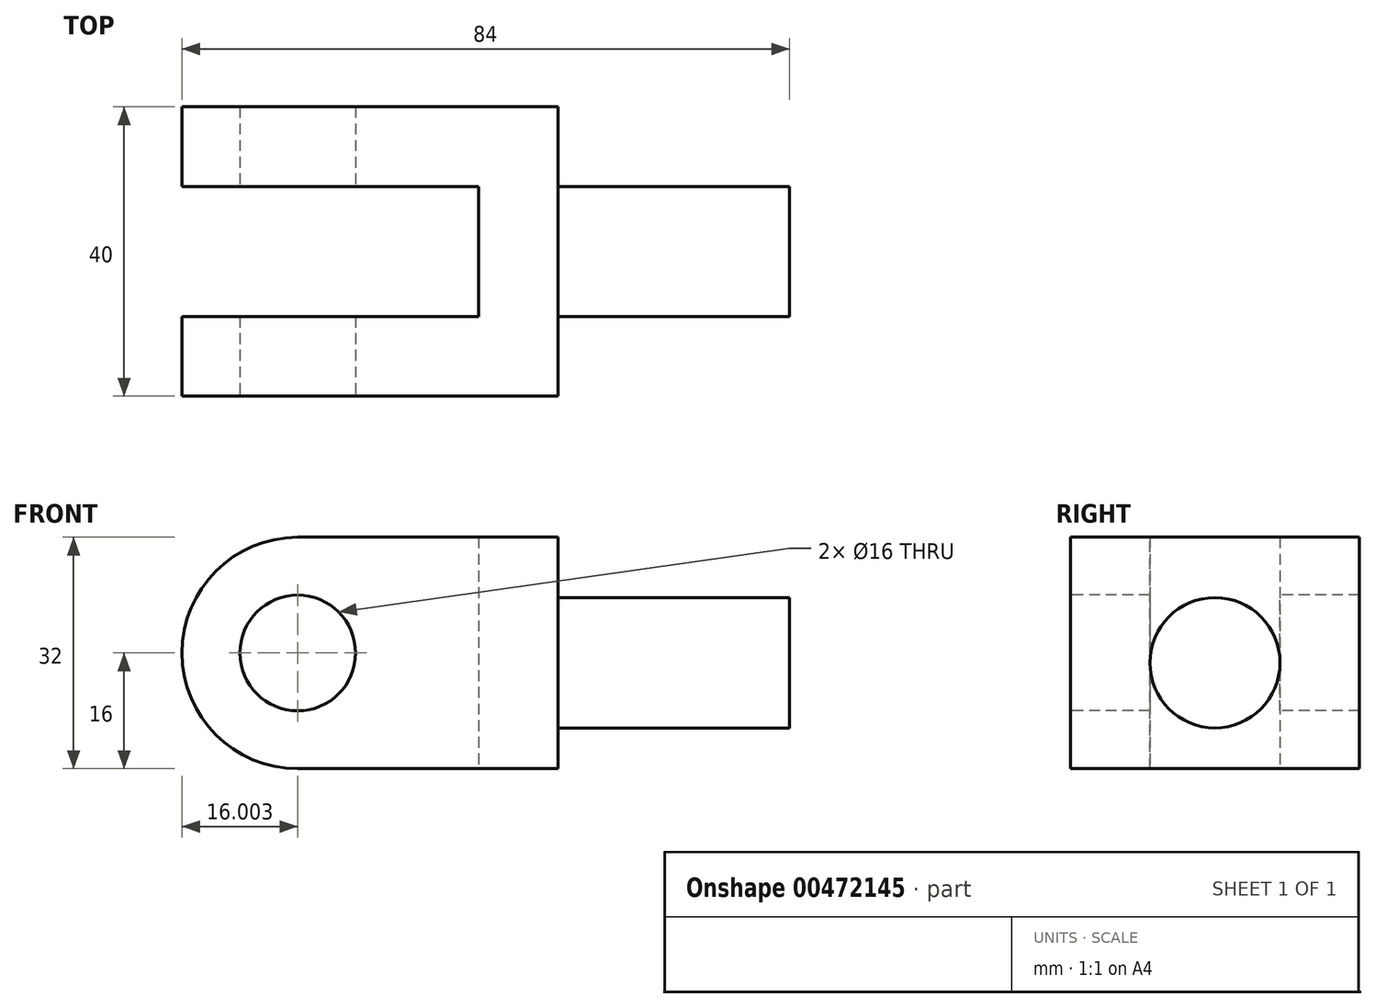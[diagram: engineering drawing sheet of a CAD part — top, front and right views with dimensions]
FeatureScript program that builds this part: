
annotation { "Feature Type Name" : "Feature", "Feature Type Description" : "" }
export const myFeature = defineFeature(function(context is Context, id is Id, definition is map)
    precondition{}
    {
        {
            var Q0;
            Q0=qCreatedBy(makeId("Top.planeOp"),FACE);
            var sketch = newSketch(context, id + "F0", { "sketchPlane" : qUnion([Q0])});
            skLineSegment(sketch, "E0", {"start": v(-54.68, 43.17) * mm, "end": v(-54.68, 32.17) * mm});
            skLineSegment(sketch, "E1", {"start": v(-54.68, 14.17) * mm, "end": v(-54.68, 3.17) * mm});
            skLineSegment(sketch, "E2", {"start": v(-54.68, 3.17) * mm, "end": v(-2.68, 3.17) * mm});
            skLineSegment(sketch, "E3", {"start": v(-2.68, 3.17) * mm, "end": v(-2.68, 43.17) * mm});
            skLineSegment(sketch, "E4", {"start": v(-2.68, 43.17) * mm, "end": v(-54.68, 43.17) * mm});
            skLineSegment(sketch, "E5", {"start": v(-2.68, 3.17) * mm, "end": v(-13.68, 3.17) * mm});
            skLineSegment(sketch, "E6", {"start": v(-54.68, 14.17) * mm, "end": v(-13.68, 14.17) * mm});
            skLineSegment(sketch, "E7", {"start": v(-13.68, 14.17) * mm, "end": v(-13.68, 32.17) * mm});
            skLineSegment(sketch, "E8", {"start": v(-13.68, 32.17) * mm, "end": v(-54.68, 32.17) * mm});
            skPoint(sketch, "E9.end.orphan", {"position": v(-13.68, 12.5) * mm});
            skLineSegment(sketch, "E10", {"start": v(-2.68, 14.17) * mm, "end": v(29.32, 14.17) * mm});
            skLineSegment(sketch, "E11", {"start": v(29.32, 14.17) * mm, "end": v(29.32, 32.17) * mm});
            skLineSegment(sketch, "E12", {"start": v(29.32, 32.17) * mm, "end": v(-2.68, 32.17) * mm});
            skSolve(sketch);
        }
        {
            var Q0;
            Q0=makeQuery(id+"F0.imprint","IMPRINT",FACE,{"disambiguationData":[TD([[makeQuery(id+"F0.imprint","IMPRINT",EDGE,{"derivedFrom":sQuery(id+"F0.wireOp",EDGE,"E0")}),1.0]])]});
            extrude(context, id + "F1", {"entities" : qUnion([Q0]), "depth" : 32 * mm});
        }
        {
            var Q0;
            Q0=makeQuery(id+"F1.opExtrude","SWEPT_FACE",FACE,{"disambiguationData":[OSD([sQuery(id+"F0.wireOp",EDGE,"E2"),sQuery(id+"F0.wireOp",EDGE,"E5")])]});
            var sketch = newSketch(context, id + "F2", { "sketchPlane" : qUnion([Q0])});
            skCircle(sketch, "E13", {"center": v(-38.68, 16) * mm, "radius": 16 * mm});
            skPoint(sketch, "E13.centerSnap0", {"position": v(-54.68, 16) * mm});
            skCircle(sketch, "E14", {"center": v(-38.68, 16) * mm, "radius": 8 * mm});
            skSolve(sketch);
        }
        {
            var Q0;
            {var subQ0=sQuery(id+"F2.wireOp",EDGE,"E13");var subQ1=sQuery(id+"F0.wireOp",EDGE,"E2");var subQ2=makeQuery(id+"F1.opExtrude","SWEPT_EDGE",EDGE,{"disambiguationData":[OSD([sQuery(id+"F0.wireOp",EDGE,"E1"),subQ1])]});var subQ3=makeQuery(id+"F2.imprint","INTERSECT",VERTEX,{"derivedFrom":[subQ2,subQ0]});Q0=makeQuery(id+"F2.imprint","IMPRINT",FACE,{"disambiguationData":[TD([[makeQuery(id+"F2.imprint","IMPRINT",EDGE,{"disambiguationData":[TD([[subQ3,1.0]])],"derivedFrom":subQ0}),-1.0]])]});}
            var Q1;
            {var subQ0=sQuery(id+"F2.wireOp",EDGE,"E13");var subQ1=sQuery(id+"F0.wireOp",EDGE,"E2");var subQ2=makeQuery(id+"F1.opExtrude","SWEPT_EDGE",EDGE,{"disambiguationData":[OSD([sQuery(id+"F0.wireOp",EDGE,"E1"),subQ1])]});var subQ3=makeQuery(id+"F2.imprint","INTERSECT",VERTEX,{"derivedFrom":[subQ2,subQ0]});Q1=makeQuery(id+"F2.imprint","IMPRINT",FACE,{"disambiguationData":[TD([[makeQuery(id+"F2.imprint","IMPRINT",EDGE,{"disambiguationData":[TD([[subQ3,-1.0]])],"derivedFrom":subQ0}),-1.0]])]});}
            var Q2;
            Q2=makeQuery(id+"F2.imprint","IMPRINT",FACE,{"disambiguationData":[TD([[makeQuery(id+"F2.imprint","IMPRINT",EDGE,{"derivedFrom":sQuery(id+"F2.wireOp",EDGE,"E14")}),1.0]])]});
            extrude(context, id + "F3", {"entities" : qUnion([Q0, Q1, Q2]), "operationType" : NewBodyOperationType.REMOVE, "oppositeDirection" : true, "depth" : 100 * mm});
        }
        {
            var Q0;
            Q0=makeQuery(id+"F1.opExtrude","SWEPT_FACE",FACE,{"disambiguationData":[OSD([sQuery(id+"F0.wireOp",EDGE,"E3")])]});
            var sketch = newSketch(context, id + "F4", { "sketchPlane" : qUnion([Q0])});
            skCircle(sketch, "E15", {"center": v(23.17, 14.64) * mm, "radius": 9 * mm});
            skLineSegment(sketch, "E16", {"start": v(23.17, 32) * mm, "end": v(23.17, 0) * mm});
            skSolve(sketch);
        }
        {
            var Q0;
            Q0 = qSketchRegion(id + "F4", true);
            extrude(context, id + "F5", {"entities" : qUnion([Q0]), "depth" : 32 * mm});
        }
    });
